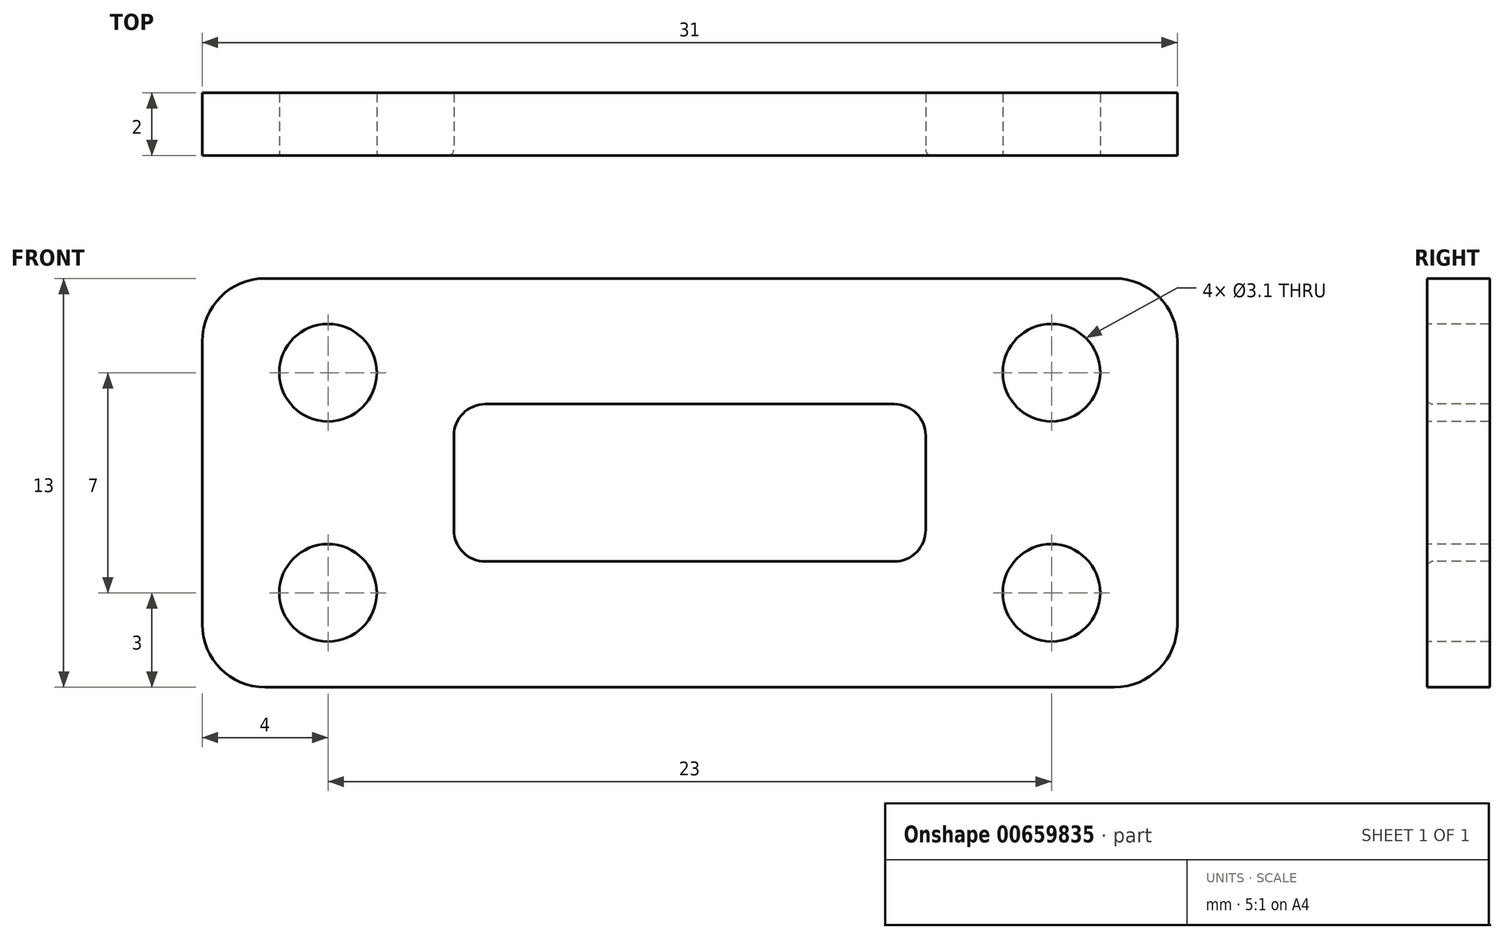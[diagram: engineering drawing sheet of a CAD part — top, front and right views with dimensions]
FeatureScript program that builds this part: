
annotation { "Feature Type Name" : "Feature", "Feature Type Description" : "" }
export const myFeature = defineFeature(function(context is Context, id is Id, definition is map)
    precondition{}
    {
        {
            var Q0;
            Q0=qCreatedBy(makeId("Front.planeOp"),FACE);
            var sketch = newSketch(context, id + "F0", { "sketchPlane" : qUnion([Q0])});
            skLineSegment(sketch, "E0.bottom", {"start": v(0, 0) * mm, "end": v(31, 0) * mm});
            skLineSegment(sketch, "E0.top", {"start": v(0, 13) * mm, "end": v(31, 13) * mm});
            skLineSegment(sketch, "E0.left", {"start": v(0, 0) * mm, "end": v(0, 13) * mm});
            skLineSegment(sketch, "E0.right", {"start": v(31, 0) * mm, "end": v(31, 13) * mm});
            skSolve(sketch);
        }
        {
            var Q0;
            Q0=qSketchRegion(id+"F0",true);
            extrude(context, id + "F1", {"entities" : qUnion([Q0]), "depth" : 2 * mm, "offsetDistance" : 25 * mm});
        }
        {
            var Q0;
            Q0=makeQuery(id+"F1.opExtrude","CAP_FACE",FACE,{"disambiguationData":[OSD([sQuery(id+"F0.wireOp",EDGE,"E0.bottom"),sQuery(id+"F0.wireOp",EDGE,"E0.top"),sQuery(id+"F0.wireOp",EDGE,"E0.left"),sQuery(id+"F0.wireOp",EDGE,"E0.right"),sQuery(id+"F0.wireOp",EDGE,"kQiuNbPG-d7aO-r9iV-VTQa-4taDSfapuuNw.bottom"),sQuery(id+"F0.wireOp",EDGE,"kQiuNbPG-d7aO-r9iV-VTQa-4taDSfapuuNw.top"),sQuery(id+"F0.wireOp",EDGE,"kQiuNbPG-d7aO-r9iV-VTQa-4taDSfapuuNw.left"),sQuery(id+"F0.wireOp",EDGE,"kQiuNbPG-d7aO-r9iV-VTQa-4taDSfapuuNw.right")])],"isStart":false});
            var sketch = newSketch(context, id + "F2", { "sketchPlane" : qUnion([Q0])});
            skCircle(sketch, "E1", {"center": v(4, 10) * mm, "radius": 1.55 * mm});
            skCircle(sketch, "E2.0.1.0", {"center": v(4, 3) * mm, "radius": 1.55 * mm});
            skCircle(sketch, "E2.1.0.0", {"center": v(27, 10) * mm, "radius": 1.55 * mm});
            skCircle(sketch, "E2.1.1.0", {"center": v(27, 3) * mm, "radius": 1.55 * mm});
            skLineSegment(sketch, "E2.direction1", {"start": v(4, 10) * mm, "end": v(27, 10) * mm, "construction": true});
            skLineSegment(sketch, "E2.direction2", {"start": v(4, 10) * mm, "end": v(4, 3) * mm, "construction": true});
            skSolve(sketch);
        }
        {
            var Q0;
            Q0=qSketchRegion(id+"F2",true);
            extrude(context, id + "F3", {"entities" : qUnion([Q0]), "operationType" : NewBodyOperationType.REMOVE, "oppositeDirection" : true, "depth" : 25 * mm, "offsetDistance" : 25 * mm});
        }
        {
            var Q0;
            Q0=makeQuery(id+"F1.opExtrude","SWEPT_EDGE",EDGE,{"disambiguationData":[OSD([sQuery(id+"F0.wireOp",EDGE,"E0.top"),sQuery(id+"F0.wireOp",EDGE,"E0.right")])]});
            var Q1;
            Q1=makeQuery(id+"F1.opExtrude","SWEPT_EDGE",EDGE,{"disambiguationData":[OSD([sQuery(id+"F0.wireOp",EDGE,"E0.bottom"),sQuery(id+"F0.wireOp",EDGE,"E0.right")])]});
            var Q2;
            Q2=makeQuery(id+"F1.opExtrude","SWEPT_EDGE",EDGE,{"disambiguationData":[OSD([sQuery(id+"F0.wireOp",EDGE,"E0.bottom"),sQuery(id+"F0.wireOp",EDGE,"E0.left")])]});
            var Q3;
            Q3=makeQuery(id+"F1.opExtrude","SWEPT_EDGE",EDGE,{"disambiguationData":[OSD([sQuery(id+"F0.wireOp",EDGE,"E0.top"),sQuery(id+"F0.wireOp",EDGE,"E0.left")])]});
            fillet(context, id + "F4", {"entities" : qUnion([Q0, Q1, Q2, Q3]), "radius" : 2 * mm, "tangentPropagation" : true, "allowEdgeOverflow" : false});
        }
        {
            var Q0;
            Q0=makeQuery(id+"F1.opExtrude","CAP_FACE",FACE,{"disambiguationData":[OSD([sQuery(id+"F0.wireOp",EDGE,"E0.bottom"),sQuery(id+"F0.wireOp",EDGE,"E0.top"),sQuery(id+"F0.wireOp",EDGE,"E0.left"),sQuery(id+"F0.wireOp",EDGE,"E0.right")])],"isStart":false});
            var sketch = newSketch(context, id + "F5", { "sketchPlane" : qUnion([Q0])});
            skLineSegment(sketch, "E3.bottom", {"start": v(8, 9) * mm, "end": v(23, 9) * mm});
            skLineSegment(sketch, "E3.top", {"start": v(8, 4) * mm, "end": v(23, 4) * mm});
            skLineSegment(sketch, "E3.left", {"start": v(8, 9) * mm, "end": v(8, 4) * mm});
            skLineSegment(sketch, "E3.right", {"start": v(23, 9) * mm, "end": v(23, 4) * mm});
            skSolve(sketch);
        }
        {
            var Q0;
            Q0=qSketchRegion(id+"F5",true);
            extrude(context, id + "F6", {"entities" : qUnion([Q0]), "operationType" : NewBodyOperationType.REMOVE, "oppositeDirection" : true, "depth" : 25 * mm, "offsetDistance" : 25 * mm});
        }
        {
            var Q0;
            Q0=makeQuery(id+"F6.boolean.opBoolean","COPY",EDGE,{"derivedFrom":makeQuery(id+"F6.opExtrude","SWEPT_EDGE",EDGE,{"disambiguationData":[OSD([sQuery(id+"F5.wireOp",EDGE,"E3.bottom"),sQuery(id+"F5.wireOp",EDGE,"E3.left")])]})});
            var Q1;
            Q1=makeQuery(id+"F6.boolean.opBoolean","COPY",EDGE,{"derivedFrom":makeQuery(id+"F6.opExtrude","SWEPT_EDGE",EDGE,{"disambiguationData":[OSD([sQuery(id+"F5.wireOp",EDGE,"E3.top"),sQuery(id+"F5.wireOp",EDGE,"E3.left")])]})});
            var Q2;
            Q2=makeQuery(id+"F6.boolean.opBoolean","COPY",EDGE,{"derivedFrom":makeQuery(id+"F6.opExtrude","SWEPT_EDGE",EDGE,{"disambiguationData":[OSD([sQuery(id+"F5.wireOp",EDGE,"E3.bottom"),sQuery(id+"F5.wireOp",EDGE,"E3.right")])]})});
            var Q3;
            Q3=makeQuery(id+"F6.boolean.opBoolean","COPY",EDGE,{"derivedFrom":makeQuery(id+"F6.opExtrude","SWEPT_EDGE",EDGE,{"disambiguationData":[OSD([sQuery(id+"F5.wireOp",EDGE,"E3.top"),sQuery(id+"F5.wireOp",EDGE,"E3.right")])]})});
            fillet(context, id + "F7", {"entities" : qUnion([Q0, Q1, Q2, Q3]), "radius" : 1 * mm, "tangentPropagation" : true, "allowEdgeOverflow" : false});
        }
        {
            var Q0;
            Q0=makeQuery(id+"F6.boolean.opBoolean","COPY",EDGE,{"derivedFrom":makeQuery(id+"F6.opExtrude","CAP_EDGE",EDGE,{"disambiguationData":[OSD([sQuery(id+"F5.wireOp",EDGE,"E3.bottom")])],"isStart":true})});
            var Q1;
            Q1=makeQuery(id+"F7.opFillet","BLEND_EDGE",EDGE,{"blendedFrom":[makeQuery(id+"F6.boolean.opBoolean","COPY",EDGE,{"derivedFrom":makeQuery(id+"F6.opExtrude","SWEPT_EDGE",EDGE,{"disambiguationData":[OSD([sQuery(id+"F5.wireOp",EDGE,"E3.bottom"),sQuery(id+"F5.wireOp",EDGE,"E3.right")])]})}),makeQuery(id+"F1.opExtrude","CAP_FACE",FACE,{"disambiguationData":[OSD([sQuery(id+"F0.wireOp",EDGE,"E0.bottom"),sQuery(id+"F0.wireOp",EDGE,"E0.top"),sQuery(id+"F0.wireOp",EDGE,"E0.left"),sQuery(id+"F0.wireOp",EDGE,"E0.right")])],"isStart":false})],"blendedInto":[makeQuery(id+"F1.opExtrude","CAP_FACE",FACE,{"disambiguationData":[OSD([sQuery(id+"F0.wireOp",EDGE,"E0.bottom"),sQuery(id+"F0.wireOp",EDGE,"E0.top"),sQuery(id+"F0.wireOp",EDGE,"E0.left"),sQuery(id+"F0.wireOp",EDGE,"E0.right")])],"isStart":false})]});
            var Q2;
            Q2=makeQuery(id+"F6.boolean.opBoolean","COPY",EDGE,{"derivedFrom":makeQuery(id+"F6.opExtrude","CAP_EDGE",EDGE,{"disambiguationData":[OSD([sQuery(id+"F5.wireOp",EDGE,"E3.right")])],"isStart":true})});
            var Q3;
            Q3=makeQuery(id+"F7.opFillet","BLEND_EDGE",EDGE,{"blendedFrom":[makeQuery(id+"F6.boolean.opBoolean","COPY",EDGE,{"derivedFrom":makeQuery(id+"F6.opExtrude","SWEPT_EDGE",EDGE,{"disambiguationData":[OSD([sQuery(id+"F5.wireOp",EDGE,"E3.top"),sQuery(id+"F5.wireOp",EDGE,"E3.right")])]})}),makeQuery(id+"F1.opExtrude","CAP_FACE",FACE,{"disambiguationData":[OSD([sQuery(id+"F0.wireOp",EDGE,"E0.bottom"),sQuery(id+"F0.wireOp",EDGE,"E0.top"),sQuery(id+"F0.wireOp",EDGE,"E0.left"),sQuery(id+"F0.wireOp",EDGE,"E0.right")])],"isStart":false})],"blendedInto":[makeQuery(id+"F1.opExtrude","CAP_FACE",FACE,{"disambiguationData":[OSD([sQuery(id+"F0.wireOp",EDGE,"E0.bottom"),sQuery(id+"F0.wireOp",EDGE,"E0.top"),sQuery(id+"F0.wireOp",EDGE,"E0.left"),sQuery(id+"F0.wireOp",EDGE,"E0.right")])],"isStart":false})]});
            var Q4;
            Q4=makeQuery(id+"F6.boolean.opBoolean","COPY",EDGE,{"derivedFrom":makeQuery(id+"F6.opExtrude","CAP_EDGE",EDGE,{"disambiguationData":[OSD([sQuery(id+"F5.wireOp",EDGE,"E3.top")])],"isStart":true})});
            var Q5;
            Q5=makeQuery(id+"F7.opFillet","BLEND_EDGE",EDGE,{"blendedFrom":[makeQuery(id+"F6.boolean.opBoolean","COPY",EDGE,{"derivedFrom":makeQuery(id+"F6.opExtrude","SWEPT_EDGE",EDGE,{"disambiguationData":[OSD([sQuery(id+"F5.wireOp",EDGE,"E3.top"),sQuery(id+"F5.wireOp",EDGE,"E3.left")])]})}),makeQuery(id+"F1.opExtrude","CAP_FACE",FACE,{"disambiguationData":[OSD([sQuery(id+"F0.wireOp",EDGE,"E0.bottom"),sQuery(id+"F0.wireOp",EDGE,"E0.top"),sQuery(id+"F0.wireOp",EDGE,"E0.left"),sQuery(id+"F0.wireOp",EDGE,"E0.right")])],"isStart":false})],"blendedInto":[makeQuery(id+"F1.opExtrude","CAP_FACE",FACE,{"disambiguationData":[OSD([sQuery(id+"F0.wireOp",EDGE,"E0.bottom"),sQuery(id+"F0.wireOp",EDGE,"E0.top"),sQuery(id+"F0.wireOp",EDGE,"E0.left"),sQuery(id+"F0.wireOp",EDGE,"E0.right")])],"isStart":false})]});
            var Q6;
            Q6=makeQuery(id+"F6.boolean.opBoolean","COPY",EDGE,{"derivedFrom":makeQuery(id+"F6.opExtrude","CAP_EDGE",EDGE,{"disambiguationData":[OSD([sQuery(id+"F5.wireOp",EDGE,"E3.left")])],"isStart":true})});
            var Q7;
            Q7=makeQuery(id+"F7.opFillet","BLEND_EDGE",EDGE,{"blendedFrom":[makeQuery(id+"F6.boolean.opBoolean","COPY",EDGE,{"derivedFrom":makeQuery(id+"F6.opExtrude","SWEPT_EDGE",EDGE,{"disambiguationData":[OSD([sQuery(id+"F5.wireOp",EDGE,"E3.bottom"),sQuery(id+"F5.wireOp",EDGE,"E3.left")])]})}),makeQuery(id+"F1.opExtrude","CAP_FACE",FACE,{"disambiguationData":[OSD([sQuery(id+"F0.wireOp",EDGE,"E0.bottom"),sQuery(id+"F0.wireOp",EDGE,"E0.top"),sQuery(id+"F0.wireOp",EDGE,"E0.left"),sQuery(id+"F0.wireOp",EDGE,"E0.right")])],"isStart":false})],"blendedInto":[makeQuery(id+"F1.opExtrude","CAP_FACE",FACE,{"disambiguationData":[OSD([sQuery(id+"F0.wireOp",EDGE,"E0.bottom"),sQuery(id+"F0.wireOp",EDGE,"E0.top"),sQuery(id+"F0.wireOp",EDGE,"E0.left"),sQuery(id+"F0.wireOp",EDGE,"E0.right")])],"isStart":false})]});
            fillet(context, id + "F8", {"entities" : qUnion([Q0, Q1, Q2, Q3, Q4, Q5, Q6, Q7]), "radius" : .2 * mm, "tangentPropagation" : true, "allowEdgeOverflow" : false});
        }
    });
